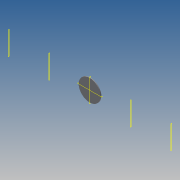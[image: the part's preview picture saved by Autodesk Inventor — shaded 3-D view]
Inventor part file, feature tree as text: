
AUTODESK INVENTOR PART (.ipt)
format: ipt  version: 2017.3 (Build 213257000, 257)  size: 96,768 bytes
history: native  units: in
note: dims shown in document units (in); Inventor stores cm internally (conversion verified against a paired STEP export)
features: plane x7, extrude x1, sketch x1, other x1
ambient origin geometry x8: Origin, YZ Plane, XZ Plane, XY Plane, X Axis, Y Axis, Z Axis, Center Point
bodies: Solid1 (feature_tree)
feature tree (10):
  plane  "Work Plane1 Centerline at surface"
  plane  "Work Plane2 Centerline at centerline"
  plane  "Work Plane3 Top"
  plane  "Work Plane4 Right"
  plane  "Work Plane5 Left"
  plane  "Work Plane6 Bottom (right)"
  plane  "Work Plane7 Bottom (left)"
  extrude  "Extrusion1"  Depth=0.5in TaperAngle=0.0deg
  sketch  "Sketch1"  dims[d0=0.0in d1=141.7323in d2=0.5in d3=0.0in d4=0.0in d5=0.0in d6=0.0in d7=26.7035in d8=-26.7035in d9=53.4071in d10=-53.4071in d11=7.0in d12=53.4071in]
  other  "2D Equation Curve1"
